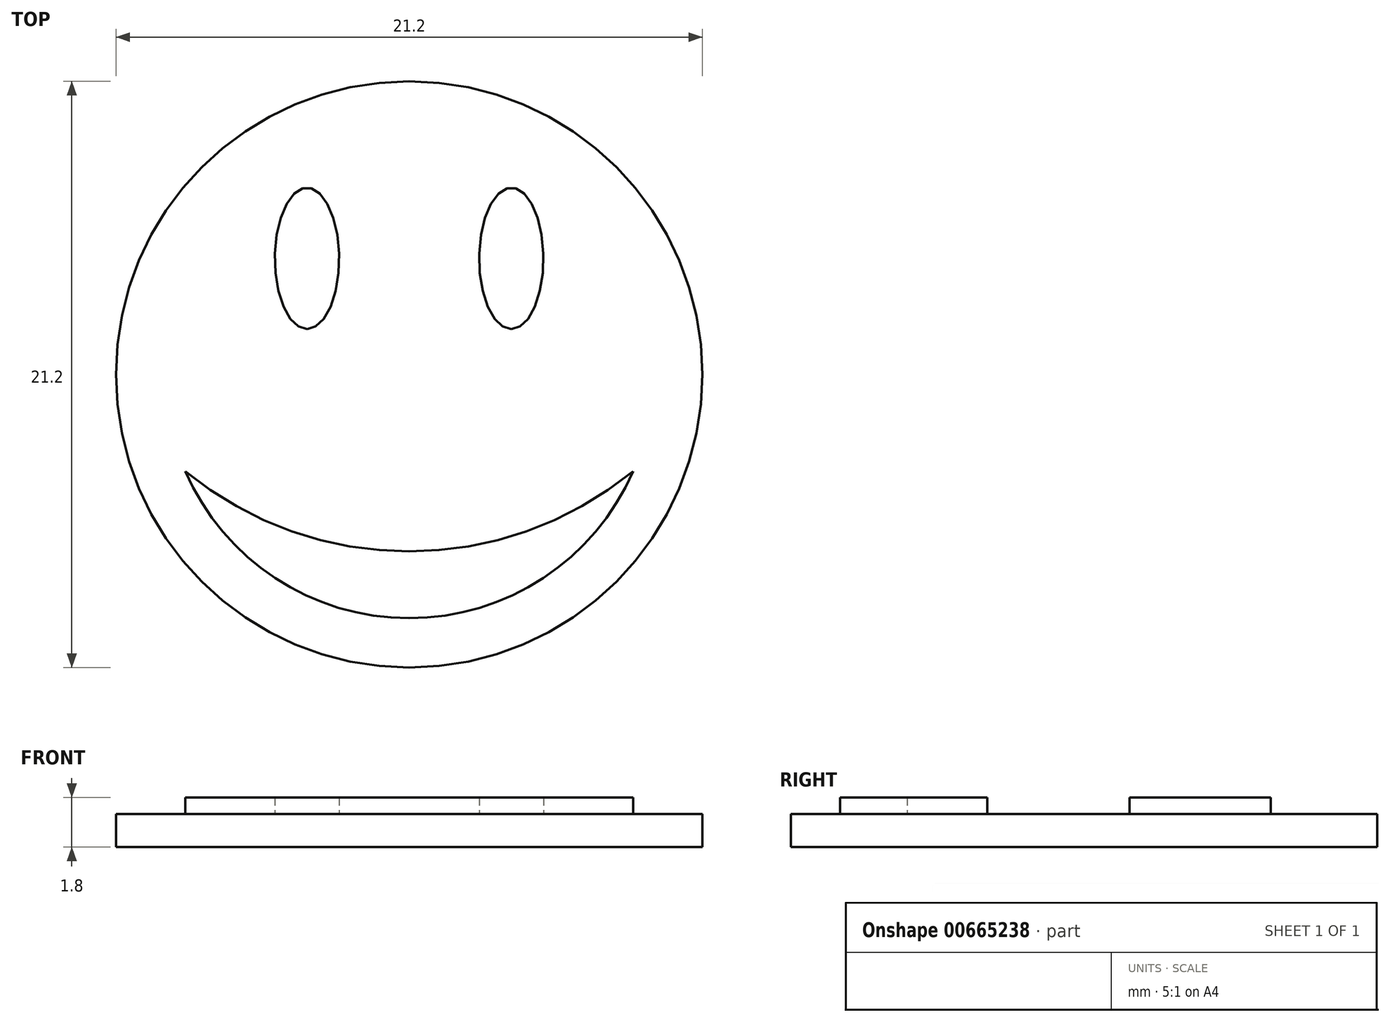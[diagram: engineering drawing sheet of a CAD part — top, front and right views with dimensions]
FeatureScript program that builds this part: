
annotation { "Feature Type Name" : "Feature", "Feature Type Description" : "" }
export const myFeature = defineFeature(function(context is Context, id is Id, definition is map)
    precondition{}
    {
        {
            var Q0;
            Q0=qCreatedBy(makeId("Top.planeOp"),FACE);
            var sketch = newSketch(context, id + "F0", { "sketchPlane" : qUnion([Q0])});
            skCircle(sketch, "E0", {"center": v(0, 0) * mm, "radius": 10.6 * mm});
            skSolve(sketch);
        }
        {
            var Q0;
            Q0 = qSketchRegion(id + "F0", true);
            extrude(context, id + "F1", {"entities" : qUnion([Q0]), "depth" : 1.2 * mm, "offsetDistance" : 25 * mm});
        }
        {
            var Q0;
            Q0=makeQuery(id+"F1.opExtrude","CAP_FACE",FACE,{"disambiguationData":[OSD([sQuery(id+"F0.wireOp",EDGE,"E0")])],"isStart":false});
            var sketch = newSketch(context, id + "F2", { "sketchPlane" : qUnion([Q0])});
            skArc(sketch, "E1", {"start": v(8.1, -3.5) * mm, "mid": v(0, -8.82) * mm, "end": v(-8.1, -3.5) * mm});
            skArc(sketch, "E2", {"start": v(-8.1, -3.5) * mm, "mid": v(0, -6.4) * mm, "end": v(8.1, -3.5) * mm});
            skEllipse(sketch, "E3", {"center": v(-3.7, 4.2) * mm, "majorRadius": 2.55 * mm, "minorRadius": 1.16 * mm, "majorAxis": v(0, -1)});
            skEllipse(sketch, "E4.MirrorC", {"center": v(3.7, 4.2) * mm, "majorRadius": 2.55 * mm, "minorRadius": 1.16 * mm, "majorAxis": v(0, -1)});
            skSolve(sketch);
        }
        {
            var Q0;
            Q0 = qSketchRegion(id + "F2", true);
            extrude(context, id + "F3", {"entities" : qUnion([Q0]), "operationType" : NewBodyOperationType.ADD, "depth" : .6 * mm, "offsetDistance" : 25 * mm});
        }
    });
